# Revit family: Fireplace_Gas_DaVinci_Linear-ST
name_source: partatom
category: Mechanical Equipment
units: mm (PartAtom-declared; Revit-internal decimal feet)

## family parameters
Classification Number = 23.40.20.34.14
Cut with Voids When Loaded = No
Host = Face
Maintain Annotation Orientation = No
Part Type = Normal
Room Calculation Point = No
Round Connector Dimension = Use Diameter
Shared = No

## types (54) — shared parameters
Assembly Code = E1090900
BTU Input Notes = BTU Input per linear foot of the Fireplace Length
Construction Details = http://www.arcat.com
Default Elevation = 0' - 0"
Description = DaVinci Linear See-Thru Gas Fireplace - as Specified
Electrical_Amperage = 7 A
Electrical_Voltage = 120 V
Keynote = 10 31 00
Manufacturer = DaVinci Custom Fireplaces , Travis Industries Division
Product Data = http://www.arcat.com
Product Properties = http://www.davincifireplace.com
Revision = R1_2017-04
Sales Information = http://www.davincifireplace.com
SpecWizard = http://www.arcat.com
Specification = http://www.arcat.com
Standards Conformance = as Specified
URL = http://www.davincifireplace.com
Unit Depth = 1' - 7 5/8"
zero-valued in all types: Expected Lifespan (Years), Maintenance Schedule (Months), Warranty Duration (Years)

## per-type parameters (varying)
| type | BTU Input per Foot | HVAC_BTU Input | Locate Air Inlet A | Locate Air Inlet B | Locate Air Inlet C | Locate Air Inlet D | Locate Exhaust A | Locate Exhaust B | Model | Opening Height | Opening Height from Base of Unit | Opening Length | Unit Height | Unit Length |
| 120 x 58 Viewing Area | 10 | 145000.0 Btu/h | 0' - 10 3/8" | 3' - 5 1/4" | 1' - 6 3/4" | 3' - 5 1/4" | 2' - 7" | 5' - 0" | Linear See-Thru Category II | 4' - 10" | 1' - 0 5/8" | 10' - 0" | 7' - 4 5/8" | 10' - 2" |
| 120 x 48 Viewing Area | 10 | 145000.0 Btu/h | 0' - 8 9/16" | 2' - 8 7/8" | 1' - 4 15/16" | 3' - 5 1/4" | 2' - 7" | 0' - 0" | Linear See-Thru Category II | 4' - 0" | 1' - 0 5/8" | 10' - 0" | 6' - 6 5/8" | 10' - 2" |
| 120 x 36 Viewing Area | 10 | 145000.0 Btu/h | 0' - 10 3/8" | 3' - 5 1/4" | 1' - 6 3/4" | 3' - 5 1/4" | 2' - 7" | 0' - 0" | Linear See-Thru Category II | 3' - 0" | 1' - 0 5/8" | 10' - 0" | 5' - 6 5/8" | 10' - 2" |
| 120 x 30 Viewing Area | 10 | 145000.0 Btu/h | 0' - 10 3/8" | 3' - 5 1/4" | 1' - 6 3/4" | 3' - 5 1/4" | 2' - 7" | 0' - 0" | Linear See-Thru Category II | 2' - 6" | 1' - 0 5/8" | 10' - 0" | 5' - 0 5/8" | 10' - 2" |
| 120 x 20 Viewing Area | 10 | 145000.0 Btu/h | 0' - 10 3/8" | 3' - 5 1/4" | 1' - 6 3/4" | 3' - 5 1/4" | 2' - 7" | 0' - 0" | Linear See-Thru Category II | 1' - 8" | 1' - 0 5/8" | 10' - 0" | 4' - 2 5/8" | 10' - 2" |
| 120 x 12 Viewing Area | 10 | 145000.0 Btu/h | 0' - 10 3/8" | 3' - 5 1/4" | 1' - 6 3/4" | 3' - 5 1/4" | 2' - 7" | 0' - 0" | Linear See-Thru Category II | 1' - 0" | 1' - 0 5/8" | 10' - 0" | 3' - 6 5/8" | 10' - 2" |
| 108 x 58 Viewing Area | 9 | 130500.0 Btu/h | 0' - 8 9/16" | 2' - 8 7/8" | 1' - 4 15/16" | 3' - 5 1/4" | 2' - 7" | 0' - 0" | Linear See-Thru Category II | 4' - 10" | 1' - 0 5/8" | 9' - 0" | 7' - 4 5/8" | 9' - 2" |
| 108 x 48 Viewing Area | 9 | 130500.0 Btu/h | 0' - 8 9/16" | 2' - 8 7/8" | 1' - 4 15/16" | 3' - 5 1/4" | 2' - 7" | 0' - 0" | Linear See-Thru Category II | 4' - 0" | 1' - 0 5/8" | 9' - 0" | 6' - 6 5/8" | 9' - 2" |
| 108 x 36 Viewing Area | 9 | 130500.0 Btu/h | 0' - 8 9/16" | 2' - 8 7/8" | 1' - 4 15/16" | 3' - 5 1/4" | 2' - 7" | 0' - 0" | Linear See-Thru Category II | 3' - 0" | 1' - 0 5/8" | 9' - 0" | 5' - 6 5/8" | 9' - 2" |
| 108 x 30 Viewing Area | 9 | 130500.0 Btu/h | 0' - 8 9/16" | 2' - 8 7/8" | 1' - 4 15/16" | 3' - 5 1/4" | 2' - 7" | 0' - 0" | Linear See-Thru Category II | 2' - 6" | 1' - 0 5/8" | 9' - 0" | 5' - 0 5/8" | 9' - 2" |
| 108 x 20 Viewing Area | 9 | 130500.0 Btu/h | 0' - 8 9/16" | 2' - 8 7/8" | 1' - 4 15/16" | 3' - 5 1/4" | 2' - 7" | 0' - 0" | Linear See-Thru Category II | 1' - 8" | 1' - 0 5/8" | 9' - 0" | 4' - 2 5/8" | 9' - 2" |
| 108 x 12 Viewing Area | 9 | 130500.0 Btu/h | 0' - 8 9/16" | 2' - 8 7/8" | 1' - 4 15/16" | 3' - 5 1/4" | 2' - 7" | 0' - 0" | Linear See-Thru Category II | 1' - 0" | 1' - 0 5/8" | 9' - 0" | 3' - 6 5/8" | 9' - 2" |
| 96 x 58 Viewing Area | 8 | 116000.0 Btu/h | 3' - 5 7/16" | 1' - 3 1/8" | 2' - 8 7/8" | 0' - 0" | 2' - 1" | 4' - 0" | Linear See-Thru Category II | 4' - 10" | 1' - 0 5/8" | 8' - 0" | 7' - 4 5/8" | 8' - 2" |
| 96 x 48 Viewing Area | 8 | 116000.0 Btu/h | 0' - 8 9/16" | 2' - 8 7/8" | 1' - 3 1/8" | 2' - 8 7/8" | 2' - 1" | 4' - 0" | Linear See-Thru Category II | 4' - 0" | 1' - 0 5/8" | 8' - 0" | 6' - 6 5/8" | 8' - 2" |
| 96 x 36 Viewing Area | 8 | 116000.0 Btu/h | 3' - 5 7/16" | 1' - 3 1/8" | 2' - 8 7/8" | 0' - 0" | 2' - 1" | 0' - 0" | Linear See-Thru Category II | 3' - 0" | 1' - 0 5/8" | 8' - 0" | 5' - 6 5/8" | 8' - 2" |
| 96 x 30 Viewing Area | 8 | 116000.0 Btu/h | 3' - 5 7/16" | 1' - 3 1/8" | 2' - 8 7/8" | 0' - 0" | 2' - 1" | 0' - 0" | Linear See-Thru Category II | 2' - 6" | 1' - 0 5/8" | 8' - 0" | 5' - 0 5/8" | 8' - 2" |
| 96 x 20 Viewing Area | 8 | 116000.0 Btu/h | 3' - 5 7/16" | 1' - 3 1/8" | 2' - 8 7/8" | 0' - 0" | 2' - 1" | 0' - 0" | Linear See-Thru Category II | 1' - 8" | 1' - 0 5/8" | 8' - 0" | 4' - 2 5/8" | 8' - 2" |
| 96 x 12 Viewing Area | 8 | 116000.0 Btu/h | 3' - 5 7/16" | 1' - 3 1/8" | 2' - 8 7/8" | 0' - 0" | 2' - 1" | 0' - 0" | Linear See-Thru Category II | 1' - 0" | 1' - 0 5/8" | 8' - 0" | 3' - 6 5/8" | 8' - 2" |
| 84 x 58 Viewing Area | 7 | 101500.0 Btu/h | 2' - 7" | 1' - 1 9/16" | 2' - 8 7/8" | 0' - 0" | 2' - 1" | 3' - 6" | Linear See-Thru Category II | 4' - 10" | 1' - 0 5/8" | 7' - 0" | 7' - 4 5/8" | 7' - 2" |
| 84 x 48 Viewing Area | 7 | 101500.0 Btu/h | 0' - 7" | 2' - 0" | 1' - 1 9/16" | 2' - 8 7/8" | 2' - 1" | 3' - 6" | Linear See-Thru Category II | 4' - 0" | 1' - 0 5/8" | 7' - 0" | 6' - 6 5/8" | 7' - 2" |
| 84 x 36 Viewing Area | 7 | 101500.0 Btu/h | 2' - 7" | 1' - 1 9/16" | 2' - 8 7/8" | 0' - 0" | 2' - 1" | 0' - 0" | Linear See-Thru Category II | 3' - 0" | 1' - 0 5/8" | 7' - 0" | 5' - 6 5/8" | 7' - 2" |
| 84 x 30 Viewing Area | 7 | 101500.0 Btu/h | 2' - 7" | 1' - 1 9/16" | 2' - 8 7/8" | 0' - 0" | 2' - 1" | 0' - 0" | Linear See-Thru Category II | 2' - 6" | 1' - 0 5/8" | 7' - 0" | 5' - 0 5/8" | 7' - 2" |
| 84 x 20 Viewing Area | 7 | 101500.0 Btu/h | 2' - 7" | 1' - 1 9/16" | 2' - 8 7/8" | 0' - 0" | 2' - 1" | 0' - 0" | Linear See-Thru Category II | 1' - 8" | 1' - 0 5/8" | 7' - 0" | 4' - 2 5/8" | 7' - 2" |
| 84 x 12 Viewing Area | 7 | 101500.0 Btu/h | 2' - 7" | 1' - 1 9/16" | 2' - 8 7/8" | 0' - 0" | 2' - 1" | 0' - 0" | Linear See-Thru Category II | 1' - 0" | 1' - 0 5/8" | 7' - 0" | 3' - 6 5/8" | 7' - 2" |
| 72 x 58 Viewing Area | 6 | 87000.0 Btu/h | 2' - 7" | 1' - 0" | 0' - 0" | 0' - 0" | 1' - 7" | 0' - 0" | Linear See-Thru Category I | 4' - 10" | 1' - 0 5/8" | 6' - 0" | 7' - 4 5/8" | 6' - 2" |
| 72 x 48 Viewing Area | 6 | 87000.0 Btu/h | 0' - 7" | 2' - 0" | 1' - 0" | 2' - 0" | 1' - 7" | 3' - 0" | Linear See-Thru Category I | 4' - 0" | 1' - 0 5/8" | 6' - 0" | 6' - 6 5/8" | 6' - 2" |
| 72 x 36 Viewing Area | 6 | 87000.0 Btu/h | 2' - 7" | 1' - 0" | 0' - 0" | 0' - 0" | 1' - 7" | 0' - 0" | Linear See-Thru Category I | 3' - 0" | 1' - 0 5/8" | 6' - 0" | 5' - 6 5/8" | 6' - 2" |
| 72 x 30 Viewing Area | 6 | 87000.0 Btu/h | 2' - 7" | 1' - 0" | 0' - 0" | 0' - 0" | 1' - 7" | 0' - 0" | Linear See-Thru Category I | 2' - 6" | 1' - 0 5/8" | 6' - 0" | 5' - 0 5/8" | 6' - 2" |
| 72 x 20 Viewing Area | 6 | 87000.0 Btu/h | 2' - 7" | 1' - 0" | 0' - 0" | 0' - 0" | 1' - 7" | 0' - 0" | Linear See-Thru Category I | 1' - 8" | 1' - 0 5/8" | 6' - 0" | 4' - 2 5/8" | 6' - 2" |
| 72 x 12 Viewing Area | 6 | 87000.0 Btu/h | 2' - 7" | 1' - 0" | 0' - 0" | 0' - 0" | 1' - 7" | 0' - 0" | Linear See-Thru Category I | 1' - 0" | 1' - 0 5/8" | 6' - 0" | 3' - 6 5/8" | 6' - 2" |
| 60 x 58 Viewing Area | 5 | 72500.0 Btu/h | 0' - 10 3/8" | 0' - 0" | 0' - 0" | 0' - 0" | 2' - 7" | 0' - 0" | Linear See-Thru Category I | 4' - 10" | 0' - 11 1/8" | 5' - 0" | 7' - 3 3/16" | 5' - 2" |
| 60 x 48 Viewing Area | 5 | 72500.0 Btu/h | 0' - 10 3/8" | 0' - 0" | 0' - 0" | 0' - 0" | 2' - 7" | 0' - 0" | Linear See-Thru Category I | 4' - 0" | 1' - 0 5/8" | 5' - 0" | 6' - 6 5/8" | 5' - 2" |
| 60 x 36 Viewing Area | 5 | 72500.0 Btu/h | 0' - 10 3/8" | 0' - 0" | 0' - 0" | 0' - 0" | 2' - 7" | 0' - 0" | Linear See-Thru Category I | 3' - 0" | 0' - 11 1/8" | 5' - 0" | 5' - 5 3/16" | 5' - 2" |
| 60 x 30 Viewing Area | 5 | 72500.0 Btu/h | 0' - 10 3/8" | 0' - 0" | 0' - 0" | 0' - 0" | 2' - 7" | 0' - 0" | Linear See-Thru Category I | 2' - 6" | 0' - 11 1/8" | 5' - 0" | 4' - 11 3/16" | 5' - 2" |
| 60 x 20 Viewing Area | 5 | 72500.0 Btu/h | 0' - 10 3/8" | 0' - 0" | 0' - 0" | 0' - 0" | 2' - 7" | 0' - 0" | Linear See-Thru Category I | 1' - 8" | 0' - 11 1/8" | 5' - 0" | 4' - 1 3/16" | 5' - 2" |
| 60 x 12 Viewing Area | 5 | 72500.0 Btu/h | 0' - 10 3/8" | 0' - 0" | 0' - 0" | 0' - 0" | 2' - 7" | 0' - 0" | Linear See-Thru Category I | 1' - 0" | 0' - 11 1/8" | 5' - 0" | 3' - 5 3/16" | 5' - 2" |
| 48 x 58 Viewing Area | 4 | 58000.0 Btu/h | 0' - 8 9/16" | 0' - 0" | 0' - 0" | 0' - 0" | 2' - 1" | 0' - 0" | Linear See-Thru Category I | 4' - 10" | 0' - 11 1/8" | 4' - 0" | 7' - 3 3/16" | 4' - 2" |
| 48 x 48 Viewing Area | 4 | 58000.0 Btu/h | 0' - 8 9/16" | 0' - 0" | 0' - 0" | 0' - 0" | 2' - 1" | 0' - 0" | Linear See-Thru Category I | 4' - 0" | 1' - 0 5/8" | 4' - 0" | 6' - 6 5/8" | 4' - 2" |
| 48 x 36 Viewing Area | 4 | 58000.0 Btu/h | 0' - 8 9/16" | 0' - 0" | 0' - 0" | 0' - 0" | 2' - 1" | 0' - 0" | Linear See-Thru Category I | 3' - 0" | 0' - 11 1/8" | 4' - 0" | 5' - 5 3/16" | 4' - 2" |
| 48 x 30 Viewing Area | 4 | 58000.0 Btu/h | 0' - 8 9/16" | 0' - 0" | 0' - 0" | 0' - 0" | 2' - 1" | 0' - 0" | Linear See-Thru Category I | 2' - 6" | 0' - 11 1/8" | 4' - 0" | 4' - 11 3/16" | 4' - 2" |
| 48 x 20 Viewing Area | 4 | 58000.0 Btu/h | 0' - 8 9/16" | 0' - 0" | 0' - 0" | 0' - 0" | 2' - 1" | 0' - 0" | Linear See-Thru Category I | 1' - 8" | 0' - 11 1/8" | 4' - 0" | 4' - 1 3/16" | 4' - 2" |
| 48 x 12 Viewing Area | 4 | 58000.0 Btu/h | 0' - 8 9/16" | 0' - 0" | 0' - 0" | 0' - 0" | 2' - 1" | 0' - 0" | Linear See-Thru Category I | 1' - 0" | 0' - 11 1/8" | 4' - 0" | 3' - 5 3/16" | 4' - 2" |
| 36 x 58 Viewing Area | 3 | 43500.0 Btu/h | 0' - 7" | 0' - 0" | 0' - 0" | 0' - 0" | 1' - 7" | 0' - 0" | Linear See-Thru Category I | 4' - 10" | 0' - 11 1/8" | 3' - 0" | 7' - 3 3/16" | 3' - 2" |
| 36 x 48 Viewing Area | 3 | 43500.0 Btu/h | 0' - 7" | 0' - 0" | 0' - 0" | 0' - 0" | 1' - 7" | 0' - 0" | Linear See-Thru Category I | 4' - 0" | 1' - 0 5/8" | 3' - 0" | 6' - 6 5/8" | 3' - 2" |
| 36 x 36 Viewing Area | 3 | 43500.0 Btu/h | 0' - 7" | 0' - 0" | 0' - 0" | 0' - 0" | 1' - 7" | 0' - 0" | Linear See-Thru Category I | 3' - 0" | 0' - 11 1/8" | 3' - 0" | 5' - 5 3/16" | 3' - 2" |
| 36 x 30 Viewing Area | 3 | 43500.0 Btu/h | 0' - 7" | 0' - 0" | 0' - 0" | 0' - 0" | 1' - 7" | 0' - 0" | Linear See-Thru Category I | 2' - 6" | 0' - 11 1/8" | 3' - 0" | 4' - 11 3/16" | 3' - 2" |
| 36 x 20 Viewing Area | 3 | 43500.0 Btu/h | 0' - 7" | 0' - 0" | 0' - 0" | 0' - 0" | 1' - 7" | 0' - 0" | Linear See-Thru Category I | 1' - 8" | 0' - 11 1/8" | 3' - 0" | 4' - 1 3/16" | 3' - 2" |
| 36 x 12 Viewing Area | 3 | 43500.0 Btu/h | 0' - 7" | 0' - 0" | 0' - 0" | 0' - 0" | 1' - 7" | 0' - 0" | Linear See-Thru Category I | 1' - 0" | 0' - 11 1/8" | 3' - 0" | 3' - 5 3/16" | 3' - 2" |
| 24 x 58 Viewing Area | 2 | 29000.0 Btu/h | 0' - 7" | 0' - 0" | 0' - 0" | 0' - 0" | 0' - 7" | 0' - 0" | Linear See-Thru Category I | 4' - 10" | 1' - 0 5/8" | 2' - 0" | 7' - 4 5/8" | 2' - 2" |
| 24 x 48 Viewing Area | 2 | 29000.0 Btu/h | 0' - 7" | 0' - 0" | 0' - 0" | 0' - 0" | 0' - 7" | 0' - 0" | Linear See-Thru Category I | 4' - 0" | 1' - 0 5/8" | 2' - 0" | 6' - 6 5/8" | 2' - 2" |
| 24 x 36 Viewing Area | 2 | 29000.0 Btu/h | 0' - 7" | 0' - 0" | 0' - 0" | 0' - 0" | 0' - 7" | 0' - 0" | Linear See-Thru Category I | 3' - 0" | 1' - 0 5/8" | 2' - 0" | 5' - 6 5/8" | 2' - 2" |
| 24 x 30 Viewing Area | 2 | 29000.0 Btu/h | 0' - 7" | 0' - 0" | 0' - 0" | 0' - 0" | 0' - 7" | 0' - 0" | Linear See-Thru Category I | 2' - 6" | 1' - 0 5/8" | 2' - 0" | 5' - 0 5/8" | 2' - 2" |
| 24 x 20 Viewing Area | 2 | 29000.0 Btu/h | 0' - 7" | 0' - 0" | 0' - 0" | 0' - 0" | 0' - 7" | 0' - 0" | Linear See-Thru Category I | 1' - 8" | 1' - 0 5/8" | 2' - 0" | 4' - 2 5/8" | 2' - 2" |
| 24 x 12 Viewing Area | 2 | 29000.0 Btu/h | 0' - 7" | 0' - 0" | 0' - 0" | 0' - 0" | 0' - 7" | 0' - 0" | Linear See-Thru Category I | 1' - 0" | 1' - 0 5/8" | 2' - 0" | 3' - 6 5/8" | 2' - 2" |

## geometry (parser evidence)
native form markers: Sweep x3
no freeform markers — native parametric forms only
